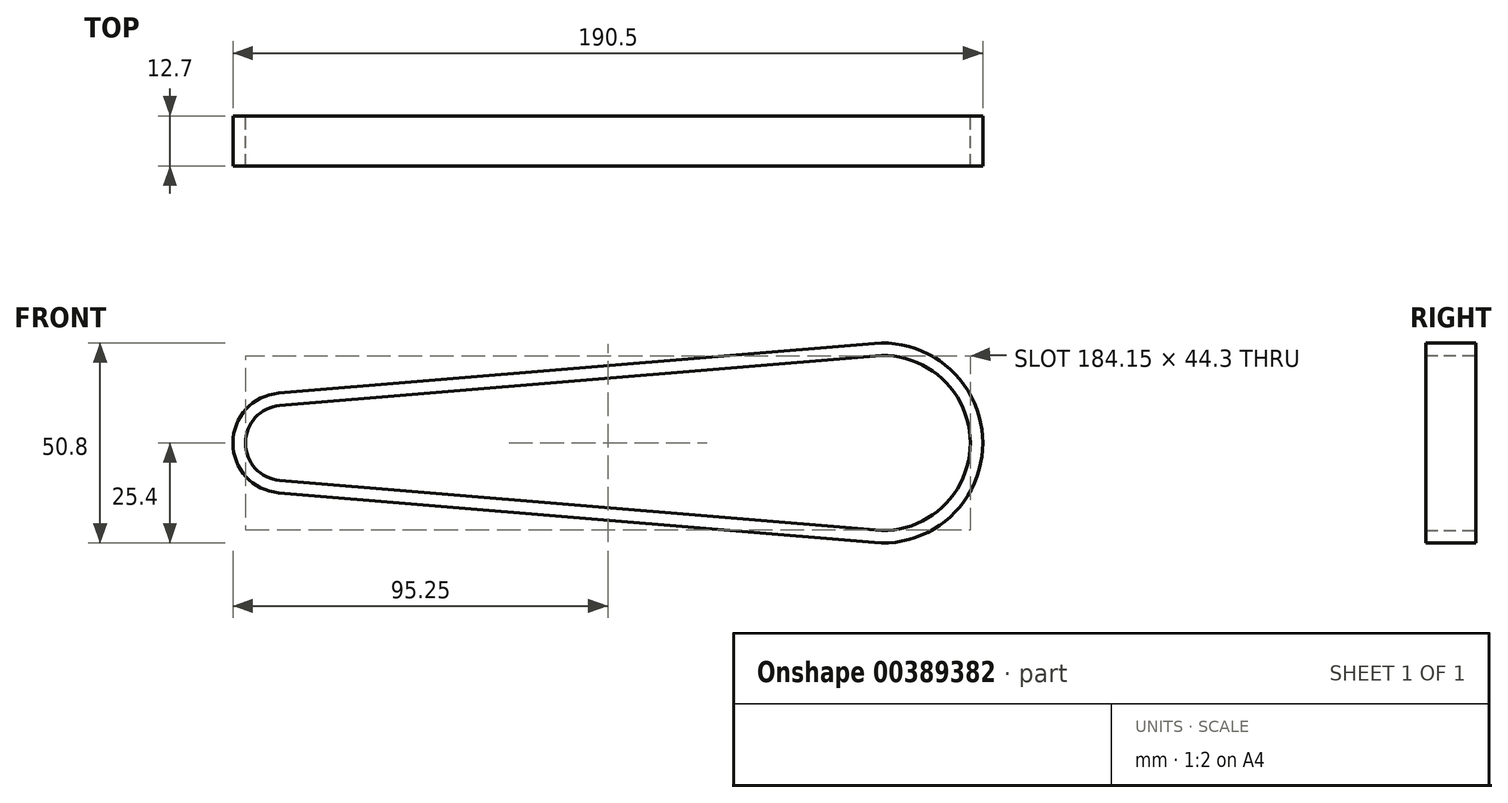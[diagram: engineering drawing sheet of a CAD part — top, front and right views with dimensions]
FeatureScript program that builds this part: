
annotation { "Feature Type Name" : "Feature", "Feature Type Description" : "" }
export const myFeature = defineFeature(function(context is Context, id is Id, definition is map)
    precondition{}
    {
        {
            var Q0;
            Q0=qCreatedBy(makeId("Front.planeOp"),FACE);
            var sketch = newSketch(context, id + "F0", { "sketchPlane" : qUnion([Q0])});
            skArc(sketch, "E0", {"start": v(-1.85, -22.15) * mm, "mid": v(22.23, 0) * mm, "end": v(-1.85, 22.15) * mm});
            skArc(sketch, "E1", {"start": v(-2.12, -25.31) * mm, "mid": v(25.4, 0) * mm, "end": v(-2.12, 25.31) * mm});
            skArc(sketch, "E2", {"start": v(-153.2, 9.5) * mm, "mid": v(-161.93, 0) * mm, "end": v(-153.2, -9.5) * mm});
            skArc(sketch, "E3", {"start": v(-153.46, 12.66) * mm, "mid": v(-165.1, 0) * mm, "end": v(-153.46, -12.66) * mm});
            skLineSegment(sketch, "E4", {"start": v(-153.46, 12.66) * mm, "end": v(-2.12, 25.31) * mm});
            skLineSegment(sketch, "E5", {"start": v(-153.46, -12.66) * mm, "end": v(-2.12, -25.31) * mm});
            skLineSegment(sketch, "E6", {"start": v(-153.2, -9.5) * mm, "end": v(-1.85, -22.15) * mm});
            skLineSegment(sketch, "E7.trimOffspring", {"start": v(-153.2, 9.5) * mm, "end": v(-1.85, 22.15) * mm});
            skSolve(sketch);
        }
        {
            var Q0;
            Q0 = qSketchRegion(id + "F0", true);
            extrude(context, id + "F1", {"entities" : qUnion([Q0]), "depth" : 12.7 * mm});
        }
    });
